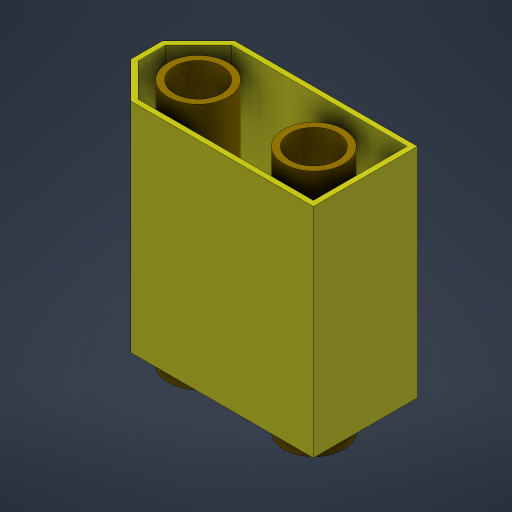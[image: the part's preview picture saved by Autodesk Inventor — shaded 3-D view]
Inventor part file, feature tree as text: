
AUTODESK INVENTOR PART (.ipt)
format: ipt  version: 2023.5 (Build 275446000, 446)  size: 209,920 bytes
history: native  units: mm
features: extrude x3, sketch x1
ambient origin geometry x8: Origin, YZ Plane, XZ Plane, XY Plane, X Axis, Y Axis, Z Axis, Center Point
bodies: Volumenkörper1 (feature_tree)
feature tree (4):
  sketch  "Skizze1"  dims[d2=20.8mm d4=45.0deg d5=9.9mm d6=3.0mm d8=5.7mm d9=11.0mm d11=4.9mm d12=0.5mm d13=4.5mm d14=20.7mm d15=0.0mm d16=23.5mm d17=0.0mm d18=15.0mm d19=0.0mm]
  extrude  "Extrusion1"  TaperAngle=45.0deg  [1 undecoded]
  extrude  "Extrusion2"  Depth=9.9mm
  extrude  "Extrusion3"  Depth=15.0mm
note: 1 required parameter value undecoded (feature->parameter linkage not recoverable at this tier; creation-order binding heuristic only, values carry confidence <= 0.55)
